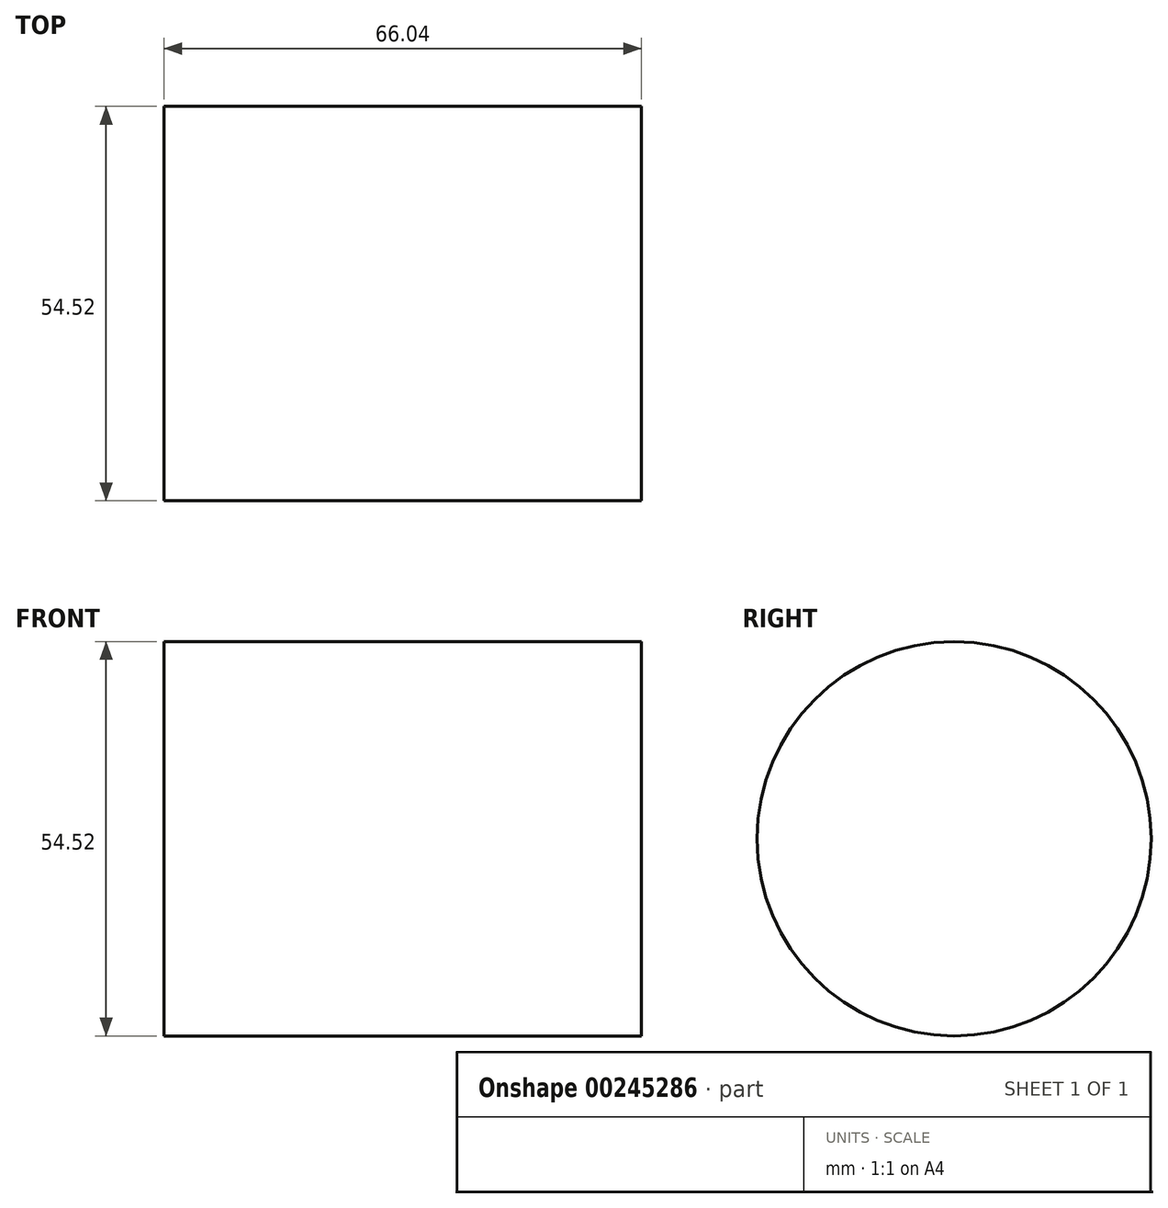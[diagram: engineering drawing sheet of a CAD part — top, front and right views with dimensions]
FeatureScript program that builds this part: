
annotation { "Feature Type Name" : "Feature", "Feature Type Description" : "" }
export const myFeature = defineFeature(function(context is Context, id is Id, definition is map)
    precondition{}
    {
        {
            var Q0;
            Q0=qCreatedBy(makeId("Right.planeOp"),FACE);
            var sketch = newSketch(context, id + "F0", { "sketchPlane" : qUnion([Q0])});
            skCircle(sketch, "E0", {"center": v(0, 0) * mm, "radius": 27.26 * mm});
            skSolve(sketch);
        }
        {
            var Q0;
            Q0 = qSketchRegion(id + "F0", true);
            extrude(context, id + "F1", {"entities" : qUnion([Q0]), "depth" : 66.04 * mm});
        }
    });
